# Revit family: Cabinet-Hardware_Pyramid-Pull
name_source: partatom
category: Casework
units: mm (PartAtom-declared; Revit-internal decimal feet)

## family parameters
Classification Number = 23.40.35.11.11
Cut with Voids When Loaded = No
Host = Face
Room Calculation Point = No
Shared = Yes

## types (1)
- Drawer-Pull
    Assembly Code = E2010200
    Construction Details = http://www.arcat.com
    Default Elevation = 4' - 0"
    Description = Drawer / Door Pull - Pyramid Shaped
    Door Slab Thickness = 0' - 0 1/2"
    Expected Lifespan (Years) = 0
    Fastener Material = ARCAT - Metal - Steel - ASTM A992
    Fastener Type = #8 Phillips Pan Head Machine Screw - Length by door thickness
    Green Building-LEED = http://www.arcat.com
    Handle Width = 0' - 1 1/2"
    Hardware Finish = ARCAT - Metal - Brass, Polished
    Hardware Finish Accent = ARCAT - Metal - Bronze, Oil Rubbed
    Hole Size = 0' - 0 3/16"
    Keynote = 12300
    Maintenance Schedule (Months) = 0
    Manufacturer = Generic
    Manufacturer Fax = (203) 929-2444
    Manufacturer Website = http://www.arcat.com
    Model = Generic
    Product Data = http://www.arcat.com
    Product Properties = http://www.arcat.com
    Specification = http://www.arcat.com
    Warranty Duration (Years) = 0

## geometry (parser evidence)
native form markers: Sweep x5
no freeform markers — native parametric forms only
